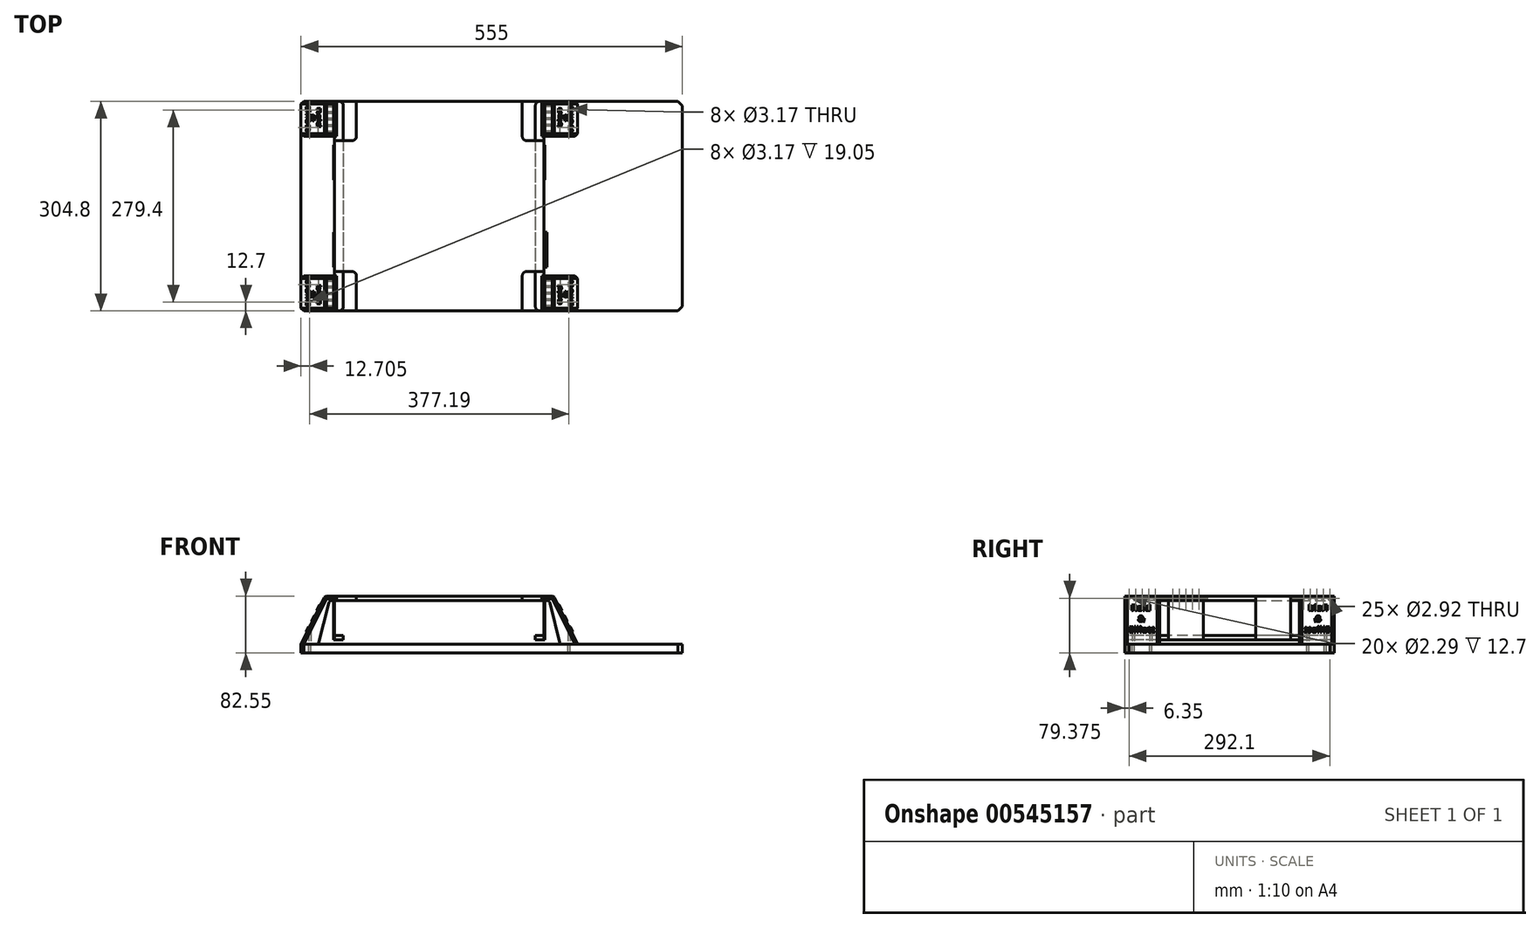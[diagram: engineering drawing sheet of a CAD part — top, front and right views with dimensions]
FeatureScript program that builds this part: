
annotation { "Feature Type Name" : "Feature", "Feature Type Description" : "" }
export const myFeature = defineFeature(function(context is Context, id is Id, definition is map)
    precondition{}
    {
        {
            var Q0;
            Q0=qCreatedBy(makeId("Top.planeOp"),FACE);
            var sketch = newSketch(context, id + "F0", { "sketchPlane" : qUnion([Q0])});
            skLineSegment(sketch, "E0.bottom", {"start": v(152.4, -152.4) * mm, "end": v(-152.4, -152.4) * mm});
            skLineSegment(sketch, "E0.top", {"start": v(152.4, 152.4) * mm, "end": v(-152.4, 152.4) * mm});
            skLineSegment(sketch, "E0.left", {"start": v(152.4, -152.4) * mm, "end": v(152.4, 152.4) * mm});
            skLineSegment(sketch, "E0.right", {"start": v(-152.4, -152.4) * mm, "end": v(-152.4, 152.4) * mm});
            skPoint(sketch, "E0.middle", {"position": v(0, 0) * mm});
            skSolve(sketch);
        }
        {
            var Q0;
            Q0 = qSketchRegion(id + "F0", true);
            extrude(context, id + "F1", {"entities" : qUnion([Q0]), "oppositeDirection" : true, "depth" : 6.35 * mm, "offsetDistance" : 25.4 * mm});
        }
        {
            var Q0;
            Q0=makeQuery(id+"F1.opExtrude","CAP_FACE",FACE,{"disambiguationData":[OSD([sQuery(id+"F0.wireOp",EDGE,"E0.bottom"),sQuery(id+"F0.wireOp",EDGE,"E0.top"),sQuery(id+"F0.wireOp",EDGE,"E0.left"),sQuery(id+"F0.wireOp",EDGE,"E0.right")])],"isStart":true});
            var sketch = newSketch(context, id + "F2", { "sketchPlane" : qUnion([Q0])});
            skLineSegment(sketch, "E1", {"start": v(0, 38.07) * mm, "end": v(0, 0) * mm});
            skLineSegment(sketch, "E2", {"start": v(0, 0) * mm, "end": v(38.7, 0) * mm});
            skLineSegment(sketch, "E3.bottom", {"start": v(-152.4, 152.4) * mm, "end": v(-153.67, 152.4) * mm});
            skLineSegment(sketch, "E3.top", {"start": v(-152.4, 101.6) * mm, "end": v(-153.67, 101.6) * mm});
            skLineSegment(sketch, "E3.left", {"start": v(-152.4, 152.4) * mm, "end": v(-152.4, 101.6) * mm});
            skLineSegment(sketch, "E3.right", {"start": v(-153.67, 152.4) * mm, "end": v(-153.67, 101.6) * mm});
            skLineSegment(sketch, "E4.MirrorCS", {"start": v(152.4, 101.6) * mm, "end": v(153.67, 101.6) * mm});
            skLineSegment(sketch, "E5.MirrorCS", {"start": v(152.4, 152.4) * mm, "end": v(153.67, 152.4) * mm});
            skLineSegment(sketch, "E6.MirrorCS", {"start": v(153.67, 152.4) * mm, "end": v(153.67, 101.6) * mm});
            skLineSegment(sketch, "E7.MirrorCS", {"start": v(152.4, 152.4) * mm, "end": v(152.4, 101.6) * mm});
            skLineSegment(sketch, "E8.MirrorCS", {"start": v(-152.4, -101.6) * mm, "end": v(-153.67, -101.6) * mm});
            skLineSegment(sketch, "E9.MirrorCS", {"start": v(-152.4, -152.4) * mm, "end": v(-153.67, -152.4) * mm});
            skLineSegment(sketch, "E10.MirrorCS", {"start": v(152.4, -101.6) * mm, "end": v(153.67, -101.6) * mm});
            skLineSegment(sketch, "E11.MirrorCS", {"start": v(152.4, -152.4) * mm, "end": v(153.67, -152.4) * mm});
            skLineSegment(sketch, "E12.MirrorCS", {"start": v(-152.4, -152.4) * mm, "end": v(-152.4, -101.6) * mm});
            skLineSegment(sketch, "E13.MirrorCS", {"start": v(-153.67, -152.4) * mm, "end": v(-153.67, -101.6) * mm});
            skLineSegment(sketch, "E14.MirrorCS", {"start": v(153.67, -152.4) * mm, "end": v(153.67, -101.6) * mm});
            skLineSegment(sketch, "E15.MirrorCS", {"start": v(152.4, -152.4) * mm, "end": v(152.4, -101.6) * mm});
            skLineSegment(sketch, "E16.bottom", {"start": v(-152.4, 88.9) * mm, "end": v(-153.67, 88.9) * mm});
            skLineSegment(sketch, "E16.top", {"start": v(-152.4, 38.1) * mm, "end": v(-153.67, 38.1) * mm});
            skLineSegment(sketch, "E16.left", {"start": v(-152.4, 88.9) * mm, "end": v(-152.4, 38.1) * mm});
            skLineSegment(sketch, "E16.right", {"start": v(-153.67, 88.9) * mm, "end": v(-153.67, 38.1) * mm});
            skLineSegment(sketch, "E17.MirrorCS", {"start": v(152.4, 38.1) * mm, "end": v(153.67, 38.1) * mm});
            skLineSegment(sketch, "E18.MirrorCS", {"start": v(152.4, 88.9) * mm, "end": v(153.67, 88.9) * mm});
            skLineSegment(sketch, "E19.MirrorCS", {"start": v(152.4, 88.9) * mm, "end": v(152.4, 38.1) * mm});
            skLineSegment(sketch, "E20.MirrorCS", {"start": v(153.67, 88.9) * mm, "end": v(153.67, 38.1) * mm});
            skLineSegment(sketch, "E21.MirrorCS", {"start": v(-152.4, -88.9) * mm, "end": v(-153.67, -88.9) * mm});
            skLineSegment(sketch, "E22.MirrorCS", {"start": v(-152.4, -38.1) * mm, "end": v(-153.67, -38.1) * mm});
            skLineSegment(sketch, "E23.MirrorCS", {"start": v(152.4, -88.9) * mm, "end": v(153.67, -88.9) * mm});
            skLineSegment(sketch, "E24.MirrorCS", {"start": v(152.4, -38.1) * mm, "end": v(153.67, -38.1) * mm});
            skLineSegment(sketch, "E25.MirrorCS", {"start": v(-152.4, -88.9) * mm, "end": v(-152.4, -38.1) * mm});
            skLineSegment(sketch, "E26.MirrorCS", {"start": v(153.67, -88.9) * mm, "end": v(153.67, -38.1) * mm});
            skLineSegment(sketch, "E27.MirrorCS", {"start": v(-153.67, -88.9) * mm, "end": v(-153.67, -38.1) * mm});
            skLineSegment(sketch, "E28.MirrorCS", {"start": v(152.4, -88.9) * mm, "end": v(152.4, -38.1) * mm});
            skSolve(sketch);
        }
        {
            var Q0;
            Q0 = qSketchRegion(id + "F2", true);
            extrude(context, id + "F3", {"entities" : qUnion([Q0]), "oppositeDirection" : true, "depth" : 63.5 * mm, "offsetDistance" : 25.4 * mm});
        }
        {
            var Q0;
            Q0=makeQuery(id+"F3.opExtrude","SWEPT_FACE",FACE,{"disambiguationData":[OSD([sQuery(id+"F2.wireOp",EDGE,"E9.MirrorCS")])]});
            var sketch = newSketch(context, id + "F4", { "sketchPlane" : qUnion([Q0])});
            skLineSegment(sketch, "E29.bottom", {"start": v(-152.4, -63.5) * mm, "end": v(-139.7, -63.5) * mm});
            skLineSegment(sketch, "E29.top", {"start": v(-152.4, -57.15) * mm, "end": v(-139.7, -57.15) * mm});
            skLineSegment(sketch, "E29.left", {"start": v(-152.4, -63.5) * mm, "end": v(-152.4, -57.15) * mm});
            skLineSegment(sketch, "E29.right", {"start": v(-139.7, -63.5) * mm, "end": v(-139.7, -57.15) * mm});
            skLineSegment(sketch, "E30", {"start": v(0, -36.77) * mm, "end": v(0, 0) * mm});
            skLineSegment(sketch, "E31.MirrorCS", {"start": v(152.4, -63.5) * mm, "end": v(139.7, -63.5) * mm});
            skLineSegment(sketch, "E32.MirrorCS", {"start": v(152.4, -63.5) * mm, "end": v(152.4, -57.15) * mm});
            skLineSegment(sketch, "E33.MirrorCS", {"start": v(152.4, -57.15) * mm, "end": v(139.7, -57.15) * mm});
            skLineSegment(sketch, "E34.MirrorCS", {"start": v(139.7, -63.5) * mm, "end": v(139.7, -57.15) * mm});
            skSolve(sketch);
        }
        {
            var Q0;
            Q0 = qSketchRegion(id + "F4", true);
            var Q1;
            Q1=makeQuery(id+"F3.opExtrude","SWEPT_FACE",FACE,{"disambiguationData":[OSD([sQuery(id+"F2.wireOp",EDGE,"E3.bottom")])]});
            extrude(context, id + "F5", {"entities" : qUnion([Q0]), "endBound" : BoundingType.UP_TO_SURFACE, "oppositeDirection" : true, "depth" : 25.4 * mm, "endBoundEntityFace" : qUnion([Q1]), "offsetDistance" : 25.4 * mm});
        }
        {
            var Q0;
            Q0=makeQuery(id+"F1.opExtrude","CAP_FACE",FACE,{"disambiguationData":[OSD([sQuery(id+"F0.wireOp",EDGE,"E0.bottom"),sQuery(id+"F0.wireOp",EDGE,"E0.top"),sQuery(id+"F0.wireOp",EDGE,"E0.left"),sQuery(id+"F0.wireOp",EDGE,"E0.right")])],"isStart":true});
            var sketch = newSketch(context, id + "F6", { "sketchPlane" : qUnion([Q0])});
            skLineSegment(sketch, "E35.bottom", {"start": v(-152.4, 152.4) * mm, "end": v(-120.65, 152.4) * mm});
            skLineSegment(sketch, "E35.top", {"start": v(-152.4, 95.25) * mm, "end": v(-120.65, 95.25) * mm});
            skLineSegment(sketch, "E35.left", {"start": v(-152.4, 152.4) * mm, "end": v(-152.4, 95.25) * mm});
            skLineSegment(sketch, "E35.right", {"start": v(-120.65, 152.4) * mm, "end": v(-120.65, 95.25) * mm});
            skLineSegment(sketch, "E36", {"start": v(0, 31.85) * mm, "end": v(0, 0) * mm});
            skLineSegment(sketch, "E37", {"start": v(0, 0) * mm, "end": v(44.2, 0) * mm});
            skLineSegment(sketch, "E38.MirrorCS", {"start": v(152.4, 152.4) * mm, "end": v(120.65, 152.4) * mm});
            skLineSegment(sketch, "E39.MirrorCS", {"start": v(152.4, 95.25) * mm, "end": v(120.65, 95.25) * mm});
            skLineSegment(sketch, "E40.MirrorCS", {"start": v(152.4, 152.4) * mm, "end": v(152.4, 95.25) * mm});
            skLineSegment(sketch, "E41.MirrorCS", {"start": v(120.65, 152.4) * mm, "end": v(120.65, 95.25) * mm});
            skLineSegment(sketch, "E42.MirrorCS", {"start": v(-152.4, -152.4) * mm, "end": v(-120.65, -152.4) * mm});
            skLineSegment(sketch, "E43.MirrorCS", {"start": v(120.65, -152.4) * mm, "end": v(120.65, -95.25) * mm});
            skLineSegment(sketch, "E44.MirrorCS", {"start": v(152.4, -152.4) * mm, "end": v(152.4, -95.25) * mm});
            skLineSegment(sketch, "E45.MirrorCS", {"start": v(152.4, -95.25) * mm, "end": v(120.65, -95.25) * mm});
            skLineSegment(sketch, "E46.MirrorCS", {"start": v(-152.4, -152.4) * mm, "end": v(-152.4, -95.25) * mm});
            skLineSegment(sketch, "E47.MirrorCS", {"start": v(-152.4, -95.25) * mm, "end": v(-120.65, -95.25) * mm});
            skLineSegment(sketch, "E48.MirrorCS", {"start": v(-120.65, -152.4) * mm, "end": v(-120.65, -95.25) * mm});
            skLineSegment(sketch, "E49.MirrorCS", {"start": v(152.4, -152.4) * mm, "end": v(120.65, -152.4) * mm});
            skSolve(sketch);
        }
        {
            var Q0;
            Q0 = qSketchRegion(id + "F6", true);
            extrude(context, id + "F7", {"entities" : qUnion([Q0]), "operationType" : NewBodyOperationType.REMOVE, "endBound" : BoundingType.UP_TO_NEXT, "oppositeDirection" : true, "depth" : 25.4 * mm, "offsetDistance" : 25.4 * mm});
        }
        {
            var Q0;
            Q0=makeQuery(id+"F3.opExtrude","SWEPT_FACE",FACE,{"disambiguationData":[OSD([sQuery(id+"F2.wireOp",EDGE,"E11.MirrorCS")])]});
            var sketch = newSketch(context, id + "F8", { "sketchPlane" : qUnion([Q0])});
            skLineSegment(sketch, "E50", {"start": v(153.67, -6.35) * mm, "end": v(153.67, 0) * mm});
            skLineSegment(sketch, "E51", {"start": v(160.02, -6.35) * mm, "end": v(175.9, -69.85) * mm});
            skLineSegment(sketch, "E52", {"start": v(166.37, 0) * mm, "end": v(201.3, -69.85) * mm});
            skLineSegment(sketch, "E53", {"start": v(201.3, -69.85) * mm, "end": v(175.9, -69.85) * mm});
            skLineSegment(sketch, "E54", {"start": v(160.02, -6.35) * mm, "end": v(153.67, -6.35) * mm});
            skLineSegment(sketch, "E55", {"start": v(166.37, 0) * mm, "end": v(153.67, 0) * mm});
            skPoint(sketch, "E56.0", {"position": v(139.7, -57.15) * mm});
            skPoint(sketch, "E57", {"position": v(172.72, -57.15) * mm});
            skSolve(sketch);
        }
        {
            var Q0;
            Q0 = qSketchRegion(id + "F8", true);
            var Q1;
            Q1=makeQuery(id+"F3.opExtrude","SWEPT_FACE",FACE,{"disambiguationData":[OSD([sQuery(id+"F2.wireOp",EDGE,"E10.MirrorCS")])]});
            extrude(context, id + "F9", {"entities" : qUnion([Q0]), "endBound" : BoundingType.UP_TO_SURFACE, "oppositeDirection" : true, "depth" : 25.4 * mm, "endBoundEntityFace" : qUnion([Q1]), "offsetDistance" : 25.4 * mm});
        }
        {
            var Q0;
            Q0=makeQuery(id+"F9.opExtrude","CAP_EDGE",EDGE,{"disambiguationData":[OSD([sQuery(id+"F8.wireOp",EDGE,"E55")])],"isStart":true});
            var Q1;
            Q1=makeQuery(id+"F9.opExtrude","CAP_EDGE",EDGE,{"disambiguationData":[OSD([sQuery(id+"F8.wireOp",EDGE,"E52")])],"isStart":true});
            var Q2;
            Q2=makeQuery(id+"F9.opExtrude","SWEPT_EDGE",EDGE,{"disambiguationData":[OSD([sQuery(id+"F8.wireOp",EDGE,"E52"),sQuery(id+"F8.wireOp",EDGE,"E55")])]});
            var Q3;
            Q3=makeQuery(id+"F9.opExtrude","CAP_EDGE",EDGE,{"disambiguationData":[OSD([sQuery(id+"F8.wireOp",EDGE,"E52")])],"isStart":false});
            var Q4;
            Q4=makeQuery(id+"F9.opExtrude","CAP_EDGE",EDGE,{"disambiguationData":[OSD([sQuery(id+"F8.wireOp",EDGE,"E55")])],"isStart":false});
            chamfer(context, id + "F10", {"entities" : qUnion([Q0, Q1, Q2, Q3, Q4]), "width" : 3.8 * mm, "tangentPropagation" : true});
        }
        {
            var Q0;
            Q0=makeQuery(id+"F9.opExtrude","SWEPT_EDGE",EDGE,{"disambiguationData":[OSD([sQuery(id+"F8.wireOp",EDGE,"E51"),sQuery(id+"F8.wireOp",EDGE,"E54")])]});
            fillet(context, id + "F11", {"entities" : qUnion([Q0]), "radius" : 5.08 * mm, "tangentPropagation" : true, "allowEdgeOverflow" : false});
        }
        {
            var Q0;
            Q0=makeQuery(id+"F9.opExtrude","SWEPT_FACE",FACE,{"disambiguationData":[OSD([sQuery(id+"F8.wireOp",EDGE,"E52")])]});
            var sketch = newSketch(context, id + "F12", { "sketchPlane" : qUnion([Q0])});
            skText(sketch, "E58", { "text": " Reid\n    &\nElliott", "fontName": "OpenSans-Bold.ttf"});
            const initialGuessF12  = {"E58": [-0.14667, -0.0982, 1, 0, 0.0094]};
            skSetInitialGuess(sketch, initialGuessF12);
            skSolve(sketch);
        }
        {
            var Q0;
            Q0 = qSketchRegion(id + "F12", true);
            extrude(context, id + "F13", {"entities" : qUnion([Q0]), "operationType" : NewBodyOperationType.ADD, "depth" : 1.27 * mm, "offsetDistance" : 25.4 * mm, "hasDraft" : true, "draftAngle" : 25 * degree, "draftPullDirection" : true});
        }
        {
            var Q0;
            Q0=makeQuery(id+"F9.opExtrude","SWEPT_FACE",FACE,{"disambiguationData":[OSD([sQuery(id+"F8.wireOp",EDGE,"E50")])]});
            var sketch = newSketch(context, id + "F14", { "sketchPlane" : qUnion([Q0])});
            skLineSegment(sketch, "E59.0", {"start": v(101.6, -6.35) * mm, "end": v(152.4, -6.35) * mm});
            skLineSegment(sketch, "E60.0", {"start": v(101.6, -3.18) * mm, "end": v(152.4, -3.18) * mm});
            skCircle(sketch, "E61", {"center": v(127, -3.18) * mm, "radius": 1.14 * mm});
            skCircle(sketch, "E62.1.0.0", {"center": v(136.53, -3.18) * mm, "radius": 1.14 * mm});
            skCircle(sketch, "E62.2.0.0", {"center": v(146.05, -3.18) * mm, "radius": 1.14 * mm});
            skLineSegment(sketch, "E62.direction1", {"start": v(127, -3.18) * mm, "end": v(136.53, -3.18) * mm, "construction": true});
            skCircle(sketch, "E63.1.0.0", {"center": v(117.48, -3.18) * mm, "radius": 1.14 * mm});
            skCircle(sketch, "E63.2.0.0", {"center": v(107.95, -3.18) * mm, "radius": 1.14 * mm});
            skLineSegment(sketch, "E63.direction1", {"start": v(127, -3.18) * mm, "end": v(117.48, -3.18) * mm, "construction": true});
            skSolve(sketch);
        }
        {
            var Q0;
            Q0 = qSketchRegion(id + "F14", true);
            extrude(context, id + "F15", {"entities" : qUnion([Q0]), "operationType" : NewBodyOperationType.REMOVE, "oppositeDirection" : true, "depth" : 12.7 * mm, "offsetDistance" : 25.4 * mm});
        }
        {
            var Q0;
            Q0=makeQuery(id+"F3.opExtrude","SWEPT_FACE",FACE,{"disambiguationData":[OSD([sQuery(id+"F2.wireOp",EDGE,"E15.MirrorCS")])]});
            var sketch = newSketch(context, id + "F16", { "sketchPlane" : qUnion([Q0])});
            skLineSegment(sketch, "E64.0", {"start": v(105.41, 0) * mm, "end": v(101.6, -3.8) * mm});
            skLineSegment(sketch, "E65.0", {"start": v(105.41, 0) * mm, "end": v(148.6, 0) * mm});
            skLineSegment(sketch, "E66.0", {"start": v(152.4, -3.81) * mm, "end": v(148.6, 0) * mm});
            skLineSegment(sketch, "E67.0", {"start": v(101.6, -6.35) * mm, "end": v(152.4, -6.35) * mm});
            skLineSegment(sketch, "E68.0", {"start": v(101.6, -3.8) * mm, "end": v(101.6, -6.35) * mm});
            skLineSegment(sketch, "E69.0", {"start": v(152.4, -6.35) * mm, "end": v(152.4, -3.81) * mm});
            skCircle(sketch, "E70.0", {"center": v(107.95, -3.18) * mm, "radius": 1.14 * mm});
            skCircle(sketch, "E71", {"center": v(107.95, -3.18) * mm, "radius": 1.46 * mm});
            skCircle(sketch, "E72.1.0.0", {"center": v(117.48, -3.18) * mm, "radius": 1.46 * mm});
            skCircle(sketch, "E72.2.0.0", {"center": v(127, -3.18) * mm, "radius": 1.46 * mm});
            skCircle(sketch, "E72.3.0.0", {"center": v(136.53, -3.18) * mm, "radius": 1.46 * mm});
            skCircle(sketch, "E72.4.0.0", {"center": v(146.05, -3.18) * mm, "radius": 1.46 * mm});
            skLineSegment(sketch, "E72.direction1", {"start": v(107.95, -3.18) * mm, "end": v(117.48, -3.18) * mm, "construction": true});
            skSolve(sketch);
        }
        {
            var Q0;
            Q0 = qSketchRegion(id + "F16", true);
            extrude(context, id + "F17", {"entities" : qUnion([Q0]), "depth" : 3.17 * mm, "offsetDistance" : 25.4 * mm});
        }
        {
            var Q0;
            Q0=makeQuery(id+"F17.opExtrude","CAP_EDGE",EDGE,{"disambiguationData":[OSD([sQuery(id+"F16.wireOp",EDGE,"E71")])],"isStart":false});
            var Q1;
            Q1=makeQuery(id+"F17.opExtrude","CAP_EDGE",EDGE,{"disambiguationData":[OSD([sQuery(id+"F16.wireOp",EDGE,"E72.1.0.0")])],"isStart":false});
            var Q2;
            Q2=makeQuery(id+"F17.opExtrude","CAP_EDGE",EDGE,{"disambiguationData":[OSD([sQuery(id+"F16.wireOp",EDGE,"E72.2.0.0")])],"isStart":false});
            var Q3;
            Q3=makeQuery(id+"F17.opExtrude","CAP_EDGE",EDGE,{"disambiguationData":[OSD([sQuery(id+"F16.wireOp",EDGE,"E72.3.0.0")])],"isStart":false});
            var Q4;
            Q4=makeQuery(id+"F17.opExtrude","CAP_EDGE",EDGE,{"disambiguationData":[OSD([sQuery(id+"F16.wireOp",EDGE,"E72.4.0.0")])],"isStart":false});
            chamfer(context, id + "F18", {"entities" : qUnion([Q0, Q1, Q2, Q3, Q4]), "width" : 1.52 * mm, "tangentPropagation" : true});
        }
        {
            var Q0;
            Q0=makeQuery(id+"F9.opExtrude","SWEPT_FACE",FACE,{"disambiguationData":[OSD([sQuery(id+"F8.wireOp",EDGE,"E53")])]});
            var sketch = newSketch(context, id + "F19", { "sketchPlane" : qUnion([Q0])});
            skCircle(sketch, "E73", {"center": v(188.6, 114.3) * mm, "radius": 1.59 * mm});
            skLineSegment(sketch, "E74", {"start": v(175.9, 127) * mm, "end": v(201.3, 127) * mm});
            skLineSegment(sketch, "E75", {"start": v(188.6, 127) * mm, "end": v(188.6, 101.6) * mm});
            skCircle(sketch, "E76.MirrorC", {"center": v(188.6, 139.7) * mm, "radius": 1.59 * mm});
            skSolve(sketch);
        }
        {
            var Q0;
            Q0 = qSketchRegion(id + "F19", true);
            extrude(context, id + "F20", {"entities" : qUnion([Q0]), "operationType" : NewBodyOperationType.REMOVE, "oppositeDirection" : true, "depth" : 19.05 * mm, "offsetDistance" : 25.4 * mm});
        }
        {
            var Q0;
            Q0=makeQuery(id+"F9.opExtrude","SWEPT_BODY",BODY,{"disambiguationData":[OSD([sQuery(id+"F8.wireOp",EDGE,"E50"),sQuery(id+"F8.wireOp",EDGE,"E51"),sQuery(id+"F8.wireOp",EDGE,"E52"),sQuery(id+"F8.wireOp",EDGE,"E53"),sQuery(id+"F8.wireOp",EDGE,"E54"),sQuery(id+"F8.wireOp",EDGE,"E55")])]});
            var Q1;
            Q1=makeQuery(id+"F17.opExtrude","SWEPT_BODY",BODY,{"disambiguationData":[OSD([sQuery(id+"F16.wireOp",EDGE,"E64.0"),sQuery(id+"F16.wireOp",EDGE,"E65.0"),sQuery(id+"F16.wireOp",EDGE,"E66.0"),sQuery(id+"F16.wireOp",EDGE,"E67.0"),sQuery(id+"F16.wireOp",EDGE,"E68.0"),sQuery(id+"F16.wireOp",EDGE,"E69.0"),sQuery(id+"F16.wireOp",EDGE,"E71"),sQuery(id+"F16.wireOp",EDGE,"E72.1.0.0"),sQuery(id+"F16.wireOp",EDGE,"E72.2.0.0"),sQuery(id+"F16.wireOp",EDGE,"E72.3.0.0"),sQuery(id+"F16.wireOp",EDGE,"E72.4.0.0")])]});
            var Q2;
            Q2=qCreatedBy(makeId("Front.planeOp"),FACE);
            mirror(context, id + "F21", {"entities" : qUnion([Q0, Q1]), "mirrorPlane" : qUnion([Q2])});
        }
        {
            var Q0;
            Q0=makeQuery(id+"F9.opExtrude","SWEPT_BODY",BODY,{"disambiguationData":[OSD([sQuery(id+"F8.wireOp",EDGE,"E50"),sQuery(id+"F8.wireOp",EDGE,"E51"),sQuery(id+"F8.wireOp",EDGE,"E52"),sQuery(id+"F8.wireOp",EDGE,"E53"),sQuery(id+"F8.wireOp",EDGE,"E54"),sQuery(id+"F8.wireOp",EDGE,"E55")])]});
            var Q1;
            Q1=makeQuery(id+"F21.opPattern","COPY",BODY,{"derivedFrom":makeQuery(id+"F9.opExtrude","SWEPT_BODY",BODY,{"disambiguationData":[OSD([sQuery(id+"F8.wireOp",EDGE,"E50"),sQuery(id+"F8.wireOp",EDGE,"E51"),sQuery(id+"F8.wireOp",EDGE,"E52"),sQuery(id+"F8.wireOp",EDGE,"E53"),sQuery(id+"F8.wireOp",EDGE,"E54"),sQuery(id+"F8.wireOp",EDGE,"E55")])]}),"instanceName":"1"});
            var Q2;
            Q2=makeQuery(id+"F17.opExtrude","SWEPT_BODY",BODY,{"disambiguationData":[OSD([sQuery(id+"F16.wireOp",EDGE,"E64.0"),sQuery(id+"F16.wireOp",EDGE,"E65.0"),sQuery(id+"F16.wireOp",EDGE,"E66.0"),sQuery(id+"F16.wireOp",EDGE,"E67.0"),sQuery(id+"F16.wireOp",EDGE,"E68.0"),sQuery(id+"F16.wireOp",EDGE,"E69.0"),sQuery(id+"F16.wireOp",EDGE,"E71"),sQuery(id+"F16.wireOp",EDGE,"E72.1.0.0"),sQuery(id+"F16.wireOp",EDGE,"E72.2.0.0"),sQuery(id+"F16.wireOp",EDGE,"E72.3.0.0"),sQuery(id+"F16.wireOp",EDGE,"E72.4.0.0")])]});
            var Q3;
            Q3=makeQuery(id+"F21.opPattern","COPY",BODY,{"derivedFrom":makeQuery(id+"F17.opExtrude","SWEPT_BODY",BODY,{"disambiguationData":[OSD([sQuery(id+"F16.wireOp",EDGE,"E64.0"),sQuery(id+"F16.wireOp",EDGE,"E65.0"),sQuery(id+"F16.wireOp",EDGE,"E66.0"),sQuery(id+"F16.wireOp",EDGE,"E67.0"),sQuery(id+"F16.wireOp",EDGE,"E68.0"),sQuery(id+"F16.wireOp",EDGE,"E69.0"),sQuery(id+"F16.wireOp",EDGE,"E71"),sQuery(id+"F16.wireOp",EDGE,"E72.1.0.0"),sQuery(id+"F16.wireOp",EDGE,"E72.2.0.0"),sQuery(id+"F16.wireOp",EDGE,"E72.3.0.0"),sQuery(id+"F16.wireOp",EDGE,"E72.4.0.0")])]}),"instanceName":"1"});
            var Q4;
            Q4=qCreatedBy(makeId("Right.planeOp"),FACE);
            mirror(context, id + "F22", {"entities" : qUnion([Q0, Q1, Q2, Q3]), "mirrorPlane" : qUnion([Q4])});
        }
        {
            var Q0;
            Q0=makeQuery(id+"F7.boolean.opBoolean","COPY",EDGE,{"derivedFrom":makeQuery(id+"F7.opExtrude","SWEPT_EDGE",EDGE,{"disambiguationData":[OSD([sQuery(id+"F6.wireOp",EDGE,"E43.MirrorCS"),sQuery(id+"F6.wireOp",EDGE,"E45.MirrorCS")])]})});
            var Q1;
            Q1=makeQuery(id+"F7.boolean.opBoolean","COPY",EDGE,{"derivedFrom":makeQuery(id+"F7.opExtrude","SWEPT_EDGE",EDGE,{"disambiguationData":[OSD([sQuery(id+"F0.wireOp",EDGE,"E0.left"),sQuery(id+"F6.wireOp",EDGE,"E44.MirrorCS"),sQuery(id+"F6.wireOp",EDGE,"E45.MirrorCS")])]})});
            var Q2;
            Q2=makeQuery(id+"F7.boolean.opBoolean","COPY",EDGE,{"derivedFrom":makeQuery(id+"F7.opExtrude","SWEPT_EDGE",EDGE,{"disambiguationData":[OSD([sQuery(id+"F0.wireOp",EDGE,"E0.bottom"),sQuery(id+"F6.wireOp",EDGE,"E43.MirrorCS"),sQuery(id+"F6.wireOp",EDGE,"E49.MirrorCS")])]})});
            var Q3;
            Q3=makeQuery(id+"F7.boolean.opBoolean","COPY",EDGE,{"derivedFrom":makeQuery(id+"F7.opExtrude","SWEPT_EDGE",EDGE,{"disambiguationData":[OSD([sQuery(id+"F0.wireOp",EDGE,"E0.top"),sQuery(id+"F6.wireOp",EDGE,"E38.MirrorCS"),sQuery(id+"F6.wireOp",EDGE,"E41.MirrorCS")])]})});
            var Q4;
            Q4=makeQuery(id+"F7.boolean.opBoolean","COPY",EDGE,{"derivedFrom":makeQuery(id+"F7.opExtrude","SWEPT_EDGE",EDGE,{"disambiguationData":[OSD([sQuery(id+"F6.wireOp",EDGE,"E39.MirrorCS"),sQuery(id+"F6.wireOp",EDGE,"E41.MirrorCS")])]})});
            var Q5;
            Q5=makeQuery(id+"F7.boolean.opBoolean","COPY",EDGE,{"derivedFrom":makeQuery(id+"F7.opExtrude","SWEPT_EDGE",EDGE,{"disambiguationData":[OSD([sQuery(id+"F0.wireOp",EDGE,"E0.left"),sQuery(id+"F6.wireOp",EDGE,"E39.MirrorCS"),sQuery(id+"F6.wireOp",EDGE,"E40.MirrorCS")])]})});
            var Q6;
            Q6=makeQuery(id+"F7.boolean.opBoolean","COPY",EDGE,{"derivedFrom":makeQuery(id+"F7.opExtrude","SWEPT_EDGE",EDGE,{"disambiguationData":[OSD([sQuery(id+"F0.wireOp",EDGE,"E0.top"),sQuery(id+"F6.wireOp",EDGE,"E35.bottom"),sQuery(id+"F6.wireOp",EDGE,"E35.right")])]})});
            var Q7;
            Q7=makeQuery(id+"F7.boolean.opBoolean","COPY",EDGE,{"derivedFrom":makeQuery(id+"F7.opExtrude","SWEPT_EDGE",EDGE,{"disambiguationData":[OSD([sQuery(id+"F6.wireOp",EDGE,"E35.top"),sQuery(id+"F6.wireOp",EDGE,"E35.right")])]})});
            var Q8;
            Q8=makeQuery(id+"F7.boolean.opBoolean","COPY",EDGE,{"derivedFrom":makeQuery(id+"F7.opExtrude","SWEPT_EDGE",EDGE,{"disambiguationData":[OSD([sQuery(id+"F0.wireOp",EDGE,"E0.right"),sQuery(id+"F6.wireOp",EDGE,"E35.top"),sQuery(id+"F6.wireOp",EDGE,"E35.left")])]})});
            var Q9;
            Q9=makeQuery(id+"F7.boolean.opBoolean","COPY",EDGE,{"derivedFrom":makeQuery(id+"F7.opExtrude","SWEPT_EDGE",EDGE,{"disambiguationData":[OSD([sQuery(id+"F0.wireOp",EDGE,"E0.right"),sQuery(id+"F6.wireOp",EDGE,"E46.MirrorCS"),sQuery(id+"F6.wireOp",EDGE,"E47.MirrorCS")])]})});
            var Q10;
            Q10=makeQuery(id+"F7.boolean.opBoolean","COPY",EDGE,{"derivedFrom":makeQuery(id+"F7.opExtrude","SWEPT_EDGE",EDGE,{"disambiguationData":[OSD([sQuery(id+"F6.wireOp",EDGE,"E47.MirrorCS"),sQuery(id+"F6.wireOp",EDGE,"E48.MirrorCS")])]})});
            var Q11;
            Q11=makeQuery(id+"F7.boolean.opBoolean","COPY",EDGE,{"derivedFrom":makeQuery(id+"F7.opExtrude","SWEPT_EDGE",EDGE,{"disambiguationData":[OSD([sQuery(id+"F0.wireOp",EDGE,"E0.bottom"),sQuery(id+"F6.wireOp",EDGE,"E42.MirrorCS"),sQuery(id+"F6.wireOp",EDGE,"E48.MirrorCS")])]})});
            fillet(context, id + "F23", {"entities" : qUnion([Q0, Q1, Q2, Q3, Q4, Q5, Q6, Q7, Q8, Q9, Q10, Q11]), "radius" : 6.35 * mm, "tangentPropagation" : true, "allowEdgeOverflow" : false});
        }
        {
            var Q0;
            Q0=makeQuery(id+"F22.opPattern","COPY",FACE,{"derivedFrom":makeQuery(id+"F9.opExtrude","SWEPT_FACE",FACE,{"disambiguationData":[OSD([sQuery(id+"F8.wireOp",EDGE,"E53")])]}),"instanceName":"1"});
            var sketch = newSketch(context, id + "F24", { "sketchPlane" : qUnion([Q0])});
            skLineSegment(sketch, "E77.0", {"start": v(-197.04, 152.4) * mm, "end": v(353.7, 152.4) * mm});
            skLineSegment(sketch, "E78.0", {"start": v(-201.3, 148.6) * mm, "end": v(-197.04, 152.4) * mm});
            skLineSegment(sketch, "E79.0", {"start": v(-201.3, -148.6) * mm, "end": v(-201.3, 148.6) * mm});
            skLineSegment(sketch, "E80.0", {"start": v(-201.3, -148.6) * mm, "end": v(-197.04, -152.4) * mm});
            skLineSegment(sketch, "E81.0", {"start": v(-197.04, -152.4) * mm, "end": v(353.7, -152.4) * mm});
            skLineSegment(sketch, "E82.0", {"start": v(201.3, -105.41) * mm, "end": v(201.3, -148.6) * mm});
            skLineSegment(sketch, "E83.0", {"start": v(353.7, 152.4) * mm, "end": v(353.7, -152.4) * mm});
            skPoint(sketch, "E84.orphan", {"position": v(-201.3, 105.41) * mm});
            skPoint(sketch, "E85.orphan", {"position": v(-175.9, -152.4) * mm});
            skPoint(sketch, "E86.orphan", {"position": v(-175.9, 152.4) * mm});
            skSolve(sketch);
        }
        {
            var Q0;
            Q0 = qSketchRegion(id + "F24", true);
            extrude(context, id + "F25", {"entities" : qUnion([Q0]), "depth" : 12.7 * mm, "offsetDistance" : 25.4 * mm});
        }
        {
            var Q0;
            Q0=makeQuery(id+"F25.opExtrude","SWEPT_EDGE",EDGE,{"disambiguationData":[OSD([sQuery(id+"F24.wireOp",EDGE,"E77.0"),sQuery(id+"F24.wireOp",EDGE,"E83.0")])]});
            var Q1;
            Q1=makeQuery(id+"F25.opExtrude","SWEPT_EDGE",EDGE,{"disambiguationData":[OSD([sQuery(id+"F24.wireOp",EDGE,"E81.0"),sQuery(id+"F24.wireOp",EDGE,"E83.0")])]});
            chamfer(context, id + "F26", {"entities" : qUnion([Q0, Q1]), "width" : 6.35 * mm, "tangentPropagation" : true});
        }
        {
            var Q0;
            Q0=makeQuery(id+"F5.opExtrude","CAP_EDGE",EDGE,{"disambiguationData":[OSD([sQuery(id+"F4.wireOp",EDGE,"E34.MirrorCS")])],"isStart":false});
            var Q1;
            Q1=makeQuery(id+"F5.opExtrude","CAP_EDGE",EDGE,{"disambiguationData":[OSD([sQuery(id+"F4.wireOp",EDGE,"E29.right")])],"isStart":false});
            var Q2;
            Q2=makeQuery(id+"F5.opExtrude","CAP_EDGE",EDGE,{"disambiguationData":[OSD([sQuery(id+"F4.wireOp",EDGE,"E29.right")])],"isStart":true});
            var Q3;
            Q3=makeQuery(id+"F5.opExtrude","CAP_EDGE",EDGE,{"disambiguationData":[OSD([sQuery(id+"F4.wireOp",EDGE,"E34.MirrorCS")])],"isStart":true});
            fillet(context, id + "F27", {"entities" : qUnion([Q0, Q1, Q2, Q3]), "radius" : 6.35 * mm, "tangentPropagation" : true, "allowEdgeOverflow" : false});
        }
        {
            var Q0;
            Q0=makeQuery(id+"F22.opPattern","COPY",FACE,{"derivedFrom":makeQuery(id+"F9.opExtrude","SWEPT_FACE",FACE,{"disambiguationData":[OSD([sQuery(id+"F8.wireOp",EDGE,"E53")])]}),"instanceName":"1"});
            var sketch = newSketch(context, id + "F28", { "sketchPlane" : qUnion([Q0])});
            skCircle(sketch, "E87.0", {"center": v(-188.6, 139.7) * mm, "radius": 1.59 * mm});
            skCircle(sketch, "E88.0", {"center": v(-188.6, 114.3) * mm, "radius": 1.59 * mm});
            skCircle(sketch, "E89.0", {"center": v(-188.6, -139.7) * mm, "radius": 1.59 * mm});
            skCircle(sketch, "E90.0", {"center": v(-188.6, -114.3) * mm, "radius": 1.59 * mm});
            skCircle(sketch, "E91.0", {"center": v(188.6, -139.7) * mm, "radius": 1.59 * mm});
            skCircle(sketch, "E92.0", {"center": v(188.6, -114.3) * mm, "radius": 1.59 * mm});
            skCircle(sketch, "E93.0", {"center": v(188.6, 114.3) * mm, "radius": 1.59 * mm});
            skCircle(sketch, "E94.0", {"center": v(188.6, 139.7) * mm, "radius": 1.59 * mm});
            skSolve(sketch);
        }
        {
            var Q0;
            Q0 = qSketchRegion(id + "F28", true);
            extrude(context, id + "F29", {"entities" : qUnion([Q0]), "operationType" : NewBodyOperationType.REMOVE, "endBound" : BoundingType.UP_TO_NEXT, "depth" : 25.4 * mm, "offsetDistance" : 25.4 * mm});
        }
        {
            var Q0;
            Q0=makeQuery(id+"F3.opExtrude","SWEPT_FACE",FACE,{"disambiguationData":[OSD([sQuery(id+"F2.wireOp",EDGE,"E26.MirrorCS")])]});
            var sketch = newSketch(context, id + "F30", { "sketchPlane" : qUnion([Q0])});
            skLineSegment(sketch, "E95.0", {"start": v(-88.9, -6.35) * mm, "end": v(88.9, -6.35) * mm});
            skLineSegment(sketch, "E96.bottom", {"start": v(-38.1, 0) * mm, "end": v(-88.9, 0) * mm});
            skLineSegment(sketch, "E96.top", {"start": v(-38.1, -6.35) * mm, "end": v(-88.9, -6.35) * mm});
            skLineSegment(sketch, "E96.left", {"start": v(-38.1, 0) * mm, "end": v(-38.1, -6.35) * mm});
            skLineSegment(sketch, "E96.right", {"start": v(-88.9, 0) * mm, "end": v(-88.9, -6.35) * mm});
            skCircle(sketch, "E97", {"center": v(-82.55, -3.18) * mm, "radius": 1.46 * mm});
            skPoint(sketch, "E97.centerSnap0", {"position": v(-88.9, -3.18) * mm});
            skCircle(sketch, "E98.1.0.0", {"center": v(-73.03, -3.18) * mm, "radius": 1.46 * mm});
            skCircle(sketch, "E98.2.0.0", {"center": v(-63.5, -3.18) * mm, "radius": 1.46 * mm});
            skCircle(sketch, "E98.3.0.0", {"center": v(-53.98, -3.18) * mm, "radius": 1.46 * mm});
            skCircle(sketch, "E98.4.0.0", {"center": v(-44.45, -3.18) * mm, "radius": 1.46 * mm});
            skLineSegment(sketch, "E98.direction1", {"start": v(-82.55, -3.18) * mm, "end": v(-73.03, -3.18) * mm, "construction": true});
            skSolve(sketch);
        }
        {
            var Q0;
            Q0 = qSketchRegion(id + "F30", true);
            extrude(context, id + "F31", {"entities" : qUnion([Q0]), "depth" : 3.17 * mm, "offsetDistance" : 25.4 * mm});
        }
        {
            var Q0;
            Q0=makeQuery(id+"F31.opExtrude","CAP_EDGE",EDGE,{"disambiguationData":[OSD([sQuery(id+"F30.wireOp",EDGE,"E97")])],"isStart":false});
            var Q1;
            Q1=makeQuery(id+"F31.opExtrude","CAP_EDGE",EDGE,{"disambiguationData":[OSD([sQuery(id+"F30.wireOp",EDGE,"E98.1.0.0")])],"isStart":false});
            var Q2;
            Q2=makeQuery(id+"F31.opExtrude","CAP_EDGE",EDGE,{"disambiguationData":[OSD([sQuery(id+"F30.wireOp",EDGE,"E98.2.0.0")])],"isStart":false});
            var Q3;
            Q3=makeQuery(id+"F31.opExtrude","CAP_EDGE",EDGE,{"disambiguationData":[OSD([sQuery(id+"F30.wireOp",EDGE,"E98.3.0.0")])],"isStart":false});
            var Q4;
            Q4=makeQuery(id+"F31.opExtrude","CAP_EDGE",EDGE,{"disambiguationData":[OSD([sQuery(id+"F30.wireOp",EDGE,"E98.4.0.0")])],"isStart":false});
            chamfer(context, id + "F32", {"entities" : qUnion([Q0, Q1, Q2, Q3, Q4]), "width" : 1.52 * mm, "tangentPropagation" : true});
        }
    });
